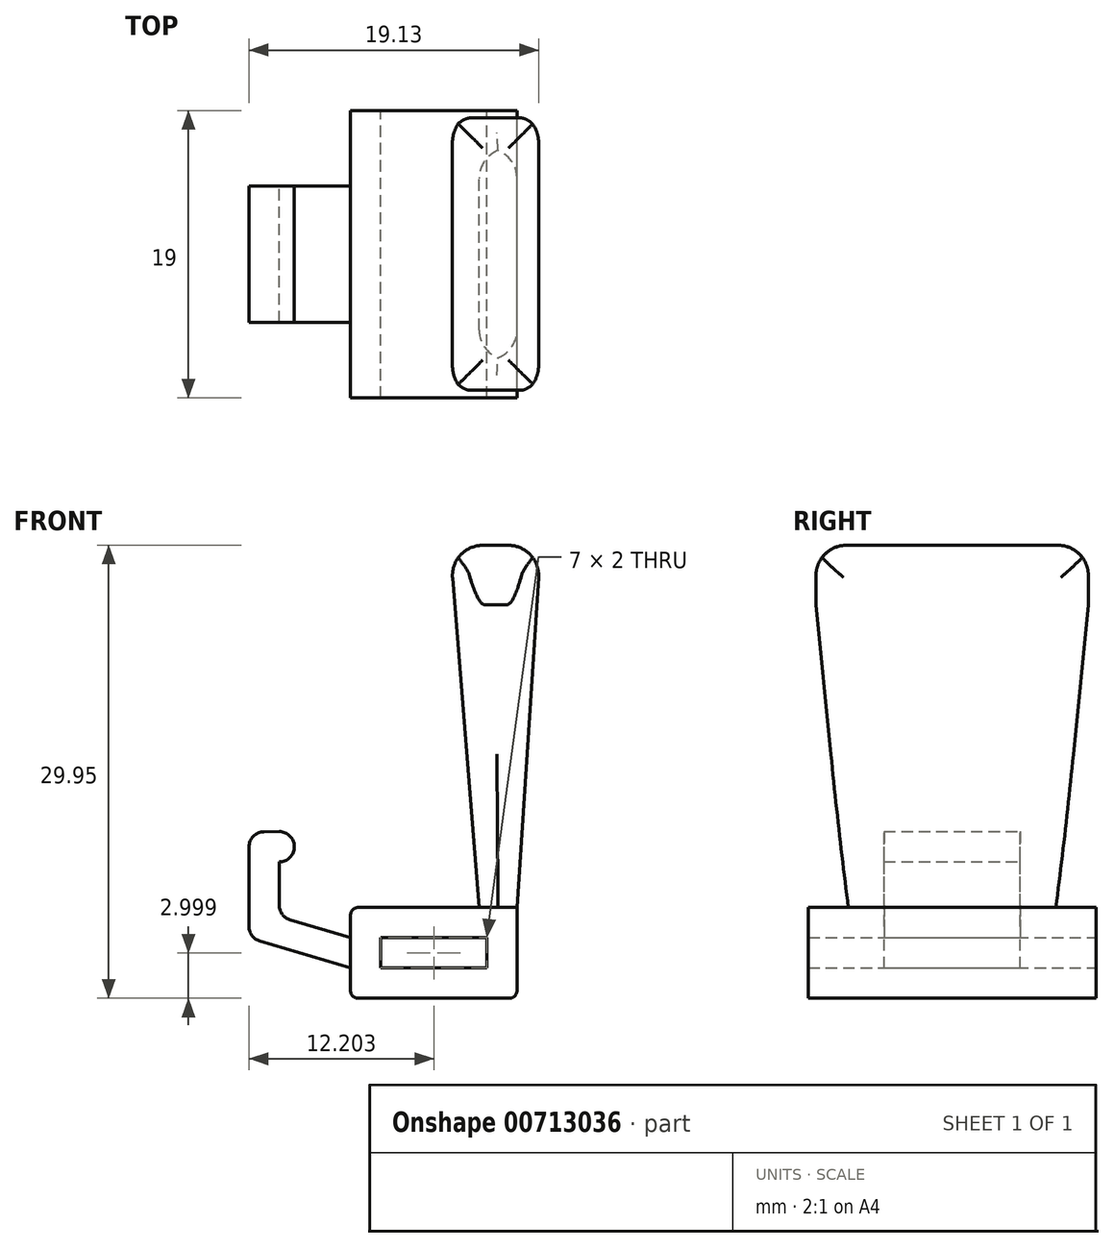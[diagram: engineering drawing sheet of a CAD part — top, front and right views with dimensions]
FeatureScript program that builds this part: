
annotation { "Feature Type Name" : "Feature", "Feature Type Description" : "" }
export const myFeature = defineFeature(function(context is Context, id is Id, definition is map)
    precondition{}
    {
        {
            var Q0;
            Q0=qCreatedBy(makeId("Front.planeOp"),FACE);
            var sketch = newSketch(context, id + "F0", { "sketchPlane" : qUnion([Q0])});
            skLineSegment(sketch, "E0.bottom", {"start": v(-19.1, 12.93) * mm, "end": v(-30.1, 12.93) * mm});
            skLineSegment(sketch, "E0.top", {"start": v(-19.1, 18.93) * mm, "end": v(-30.1, 18.93) * mm});
            skLineSegment(sketch, "E0.left", {"start": v(-19.1, 12.93) * mm, "end": v(-19.1, 18.93) * mm});
            skLineSegment(sketch, "E0.right", {"start": v(-30.1, 12.93) * mm, "end": v(-30.1, 18.93) * mm});
            skPoint(sketch, "E0.middle", {"position": v(-24.6, 15.93) * mm});
            skLineSegment(sketch, "E1.bottom", {"start": v(-21.1, 14.93) * mm, "end": v(-28.1, 14.93) * mm});
            skLineSegment(sketch, "E1.top", {"start": v(-21.1, 16.93) * mm, "end": v(-28.1, 16.93) * mm});
            skLineSegment(sketch, "E1.left", {"start": v(-21.1, 14.93) * mm, "end": v(-21.1, 16.93) * mm});
            skLineSegment(sketch, "E1.right", {"start": v(-28.1, 14.93) * mm, "end": v(-28.1, 16.93) * mm});
            skLineSegment(sketch, "E2", {"start": v(-30.1, 14.93) * mm, "end": v(-36.8, 16.93) * mm});
            skLineSegment(sketch, "E3", {"start": v(-36.8, 16.93) * mm, "end": v(-36.8, 18.93) * mm});
            skLineSegment(sketch, "E4", {"start": v(-36.8, 18.93) * mm, "end": v(-30.1, 16.93) * mm});
            skLineSegment(sketch, "E5", {"start": v(-36.8, 18.93) * mm, "end": v(-36.8, 23.93) * mm});
            skLineSegment(sketch, "E6", {"start": v(-34.8, 18.33) * mm, "end": v(-34.8, 23.95) * mm});
            skLineSegment(sketch, "E7", {"start": v(-34.8, 23.95) * mm, "end": v(-36.8, 23.93) * mm});
            skLineSegment(sketch, "E8", {"start": v(-34.8, 23.95) * mm, "end": v(-33.8, 23.95) * mm});
            skLineSegment(sketch, "E9", {"start": v(-33.8, 23.95) * mm, "end": v(-33.8, 21.95) * mm});
            skLineSegment(sketch, "E10", {"start": v(-33.8, 21.95) * mm, "end": v(-34.8, 21.95) * mm});
            skLineSegment(sketch, "E11", {"start": v(-19.1, 18.93) * mm, "end": v(-17.53, 42.88) * mm});
            skLineSegment(sketch, "E12", {"start": v(-17.53, 42.88) * mm, "end": v(-23.53, 42.88) * mm});
            skLineSegment(sketch, "E13", {"start": v(-23.53, 42.88) * mm, "end": v(-21.6, 18.96) * mm});
            skLineSegment(sketch, "E14", {"start": v(-21.6, 18.96) * mm, "end": v(-19.1, 18.93) * mm});
            skSolve(sketch);
        }
        {
            var Q0;
            {var subQ5=sQuery(id+"F0.wireOp",EDGE,"E0.bottom");Q0=makeQuery(id+"F0.imprint","IMPRINT",FACE,{"disambiguationData":[TD([[makeQuery(id+"F0.imprint","IMPRINT",EDGE,{"derivedFrom":subQ5}),-1.0]])]});}
            extrude(context, id + "F1", {"entities" : qUnion([Q0]), "endBound" : BoundingType.SYMMETRIC, "depth" : 19 * mm, "offsetDistance" : 25 * mm});
        }
        {
            var Q0;
            {var subQ0=sQuery(id+"F0.wireOp",EDGE,"E11");Q0=makeQuery(id+"F0.imprint","IMPRINT",FACE,{"disambiguationData":[TD([[makeQuery(id+"F0.imprint","IMPRINT",EDGE,{"derivedFrom":subQ0}),1.0]])]});}
            extrude(context, id + "F2", {"entities" : qUnion([Q0]), "operationType" : NewBodyOperationType.ADD, "endBound" : BoundingType.SYMMETRIC, "depth" : 18 * mm, "offsetDistance" : 25 * mm});
        }
        {
            var Q0;
            {var subQ0=sQuery(id+"F0.wireOp",EDGE,"E8");Q0=makeQuery(id+"F0.imprint","IMPRINT",FACE,{"disambiguationData":[TD([[makeQuery(id+"F0.imprint","IMPRINT",EDGE,{"derivedFrom":subQ0}),-1.0]])]});}
            var Q1;
            {var subQ5=sQuery(id+"F0.wireOp",EDGE,"E5");Q1=makeQuery(id+"F0.imprint","IMPRINT",FACE,{"disambiguationData":[TD([[makeQuery(id+"F0.imprint","IMPRINT",EDGE,{"derivedFrom":subQ5}),-1.0]])]});}
            var Q2;
            {var subQ3=sQuery(id+"F0.wireOp",EDGE,"E2");Q2=makeQuery(id+"F0.imprint","IMPRINT",FACE,{"disambiguationData":[TD([[makeQuery(id+"F0.imprint","IMPRINT",EDGE,{"derivedFrom":subQ3}),-1.0]])]});}
            extrude(context, id + "F3", {"entities" : qUnion([Q0, Q1, Q2]), "operationType" : NewBodyOperationType.ADD, "endBound" : BoundingType.SYMMETRIC, "depth" : 9 * mm, "offsetDistance" : 25 * mm});
        }
        {
            var Q0;
            Q0=makeQuery(id+"F3.opExtrude","SWEPT_EDGE",EDGE,{"disambiguationData":[OSD([sQuery(id+"F0.wireOp",EDGE,"E2"),sQuery(id+"F0.wireOp",EDGE,"E3")])]});
            var Q1;
            Q1=makeQuery(id+"F3.opExtrude","SWEPT_EDGE",EDGE,{"disambiguationData":[OSD([sQuery(id+"F0.wireOp",EDGE,"E5"),sQuery(id+"F0.wireOp",EDGE,"E7")])]});
            var Q2;
            Q2=makeQuery(id+"F3.opExtrude","SWEPT_EDGE",EDGE,{"disambiguationData":[OSD([sQuery(id+"F0.wireOp",EDGE,"E8"),sQuery(id+"F0.wireOp",EDGE,"E9")])]});
            var Q3;
            Q3=makeQuery(id+"F3.opExtrude","SWEPT_EDGE",EDGE,{"disambiguationData":[OSD([sQuery(id+"F0.wireOp",EDGE,"E9"),sQuery(id+"F0.wireOp",EDGE,"E10")])]});
            var Q4;
            Q4=makeQuery(id+"F3.opExtrude","SWEPT_EDGE",EDGE,{"disambiguationData":[OSD([sQuery(id+"F0.wireOp",EDGE,"E4"),sQuery(id+"F0.wireOp",EDGE,"E6")])]});
            fillet(context, id + "F4", {"entities" : qUnion([Q0, Q1, Q2, Q3, Q4]), "radius" : 1 * mm, "tangentPropagation" : true, "allowEdgeOverflow" : false});
        }
        {
            var Q0;
            Q0=makeQuery(id+"F2.opExtrude","CAP_EDGE",EDGE,{"disambiguationData":[OSD([sQuery(id+"F0.wireOp",EDGE,"E14")])],"isStart":false});
            var Q1;
            Q1=makeQuery(id+"F2.opExtrude","CAP_EDGE",EDGE,{"disambiguationData":[OSD([sQuery(id+"F0.wireOp",EDGE,"E14")])],"isStart":true});
            chamfer(context, id + "F5", {"entities" : qUnion([Q0, Q1]), "chamferType" : ChamferType.TWO_OFFSETS, "width1" : 20 * mm, "oppositeDirection" : false, "width2" : 2 * mm, "tangentPropagation" : true});
        }
        {
            var Q0;
            Q0=makeQuery(id+"F5.opChamfer","BLEND_EDGE",EDGE,{"blendedFrom":[makeQuery(id+"F2.opExtrude","CAP_EDGE",EDGE,{"disambiguationData":[OSD([sQuery(id+"F0.wireOp",EDGE,"E14")])],"isStart":false}),makeQuery(id+"F2.opExtrude","SWEPT_FACE",FACE,{"disambiguationData":[OSD([sQuery(id+"F0.wireOp",EDGE,"E11")])]})],"blendedInto":[makeQuery(id+"F2.opExtrude","SWEPT_FACE",FACE,{"disambiguationData":[OSD([sQuery(id+"F0.wireOp",EDGE,"E11")])]})]});
            var Q1;
            Q1=makeQuery(id+"F5.opChamfer","BLEND_EDGE",EDGE,{"blendedFrom":[makeQuery(id+"F2.opExtrude","CAP_EDGE",EDGE,{"disambiguationData":[OSD([sQuery(id+"F0.wireOp",EDGE,"E14")])],"isStart":false}),makeQuery(id+"F2.opExtrude","SWEPT_FACE",FACE,{"disambiguationData":[OSD([sQuery(id+"F0.wireOp",EDGE,"E13")])]})],"blendedInto":[makeQuery(id+"F2.opExtrude","SWEPT_FACE",FACE,{"disambiguationData":[OSD([sQuery(id+"F0.wireOp",EDGE,"E13")])]})]});
            var Q2;
            Q2=makeQuery(id+"F5.opChamfer","BLEND_EDGE",EDGE,{"blendedFrom":[makeQuery(id+"F2.opExtrude","CAP_EDGE",EDGE,{"disambiguationData":[OSD([sQuery(id+"F0.wireOp",EDGE,"E14")])],"isStart":true}),makeQuery(id+"F2.opExtrude","SWEPT_FACE",FACE,{"disambiguationData":[OSD([sQuery(id+"F0.wireOp",EDGE,"E11")])]})],"blendedInto":[makeQuery(id+"F2.opExtrude","SWEPT_FACE",FACE,{"disambiguationData":[OSD([sQuery(id+"F0.wireOp",EDGE,"E11")])]})]});
            var Q3;
            Q3=makeQuery(id+"F5.opChamfer","BLEND_EDGE",EDGE,{"blendedFrom":[makeQuery(id+"F2.opExtrude","CAP_EDGE",EDGE,{"disambiguationData":[OSD([sQuery(id+"F0.wireOp",EDGE,"E14")])],"isStart":true}),makeQuery(id+"F2.opExtrude","SWEPT_FACE",FACE,{"disambiguationData":[OSD([sQuery(id+"F0.wireOp",EDGE,"E13")])]})],"blendedInto":[makeQuery(id+"F2.opExtrude","SWEPT_FACE",FACE,{"disambiguationData":[OSD([sQuery(id+"F0.wireOp",EDGE,"E13")])]})]});
            var Q4;
            Q4=makeQuery(id+"F2.opExtrude","SWEPT_EDGE",EDGE,{"disambiguationData":[OSD([sQuery(id+"F0.wireOp",EDGE,"E11"),sQuery(id+"F0.wireOp",EDGE,"E12")])]});
            var Q5;
            Q5=makeQuery(id+"F2.opExtrude","SWEPT_EDGE",EDGE,{"disambiguationData":[OSD([sQuery(id+"F0.wireOp",EDGE,"E12"),sQuery(id+"F0.wireOp",EDGE,"E13")])]});
            var Q6;
            Q6=makeQuery(id+"F2.opExtrude","CAP_EDGE",EDGE,{"disambiguationData":[OSD([sQuery(id+"F0.wireOp",EDGE,"E12")])],"isStart":false});
            var Q7;
            Q7=makeQuery(id+"F2.opExtrude","CAP_EDGE",EDGE,{"disambiguationData":[OSD([sQuery(id+"F0.wireOp",EDGE,"E12")])],"isStart":true});
            fillet(context, id + "F6", {"entities" : qUnion([Q0, Q1, Q2, Q3, Q4, Q5, Q6, Q7]), "radius" : 2 * mm, "tangentPropagation" : true, "allowEdgeOverflow" : false});
        }
        {
            var Q0;
            Q0=makeQuery(id+"F1.opExtrude","SWEPT_EDGE",EDGE,{"disambiguationData":[OSD([sQuery(id+"F0.wireOp",EDGE,"E0.top"),sQuery(id+"F0.wireOp",EDGE,"E0.right")])]});
            var Q1;
            Q1=makeQuery(id+"F1.opExtrude","SWEPT_EDGE",EDGE,{"disambiguationData":[OSD([sQuery(id+"F0.wireOp",EDGE,"E0.bottom"),sQuery(id+"F0.wireOp",EDGE,"E0.right")])]});
            var Q2;
            Q2=makeQuery(id+"F1.opExtrude","SWEPT_EDGE",EDGE,{"disambiguationData":[OSD([sQuery(id+"F0.wireOp",EDGE,"E0.bottom"),sQuery(id+"F0.wireOp",EDGE,"E0.left")])]});
            fillet(context, id + "F7", {"entities" : qUnion([Q0, Q1, Q2]), "radius" : .5 * mm, "tangentPropagation" : true, "allowEdgeOverflow" : false});
        }
    });
